# Revit family: Storage Tank Horiz Round RGA0250-1000H
name_source: partatom
category: Mechanical Equipment
revit_build: Autodesk Revit 2017 (Build: 20190507_1515(x64)
units: mm (PartAtom-declared; Revit-internal decimal feet)

## family parameters
Always vertical = Yes
Cut with Voids When Loaded = No
Part Type = Normal
Room Calculation Point = No
Round Connector Dimension = Use Radius
Shared = No
Work Plane-Based = No

## types (7) — shared parameters
Drain Radius = 1/2"
Leg Diameter = 1 1/2"
Manufacturer = Lochinvar
SES BIM Studio # = 201364903-58
Stand Height = 7"
URL = http://www.lochinvar.com

## per-type parameters (varying)
| type | DIAMETER | End Cap | GALLON CAPACITY | HEIGHT | LENGTH | Leg Height | Manway | Radius | Stand Length | Stand Width |
| RGA0250H | 34" | 34" | 250 | 41" | 87" | 22 43/64" | No | 17" | 58" | 22 43/64" |
| RGA0300H | 40" | 40" | 300 | 47" | 76" | 26 43/64" | No | 20" | 50 43/64" | 26 43/64" |
| RGA0400H | 46" | 46" | 400 | 53" | 76" | 30 43/64" | No | 23" | 50 43/64" | 30 43/64" |
| RGA0500H | 46" | 46" | 500 | 53" | 88" | 30 43/64" | Yes | 23" | 58 43/64" | 30 43/64" |
| RGA0600H | 52" | 52" | 600 | 59" | 88" | 34 43/64" | Yes | 26" | 58 43/64" | 34 43/64" |
| RGA0700H | 52" | 52" | 700 | 59" | 100" | 34 43/64" | Yes | 26" | 66 43/64" | 34 43/64" |
| RGA1000H | 52" | 52" | 1000 | 59" | 124" | 34 43/64" | Yes | 26" | 82 43/64" | 34 43/64" |

note: column(s) folded — value = type name in every type: MODEL NO., Model

## geometry (parser evidence)
native form markers: Sweep x2
no freeform markers — native parametric forms only
